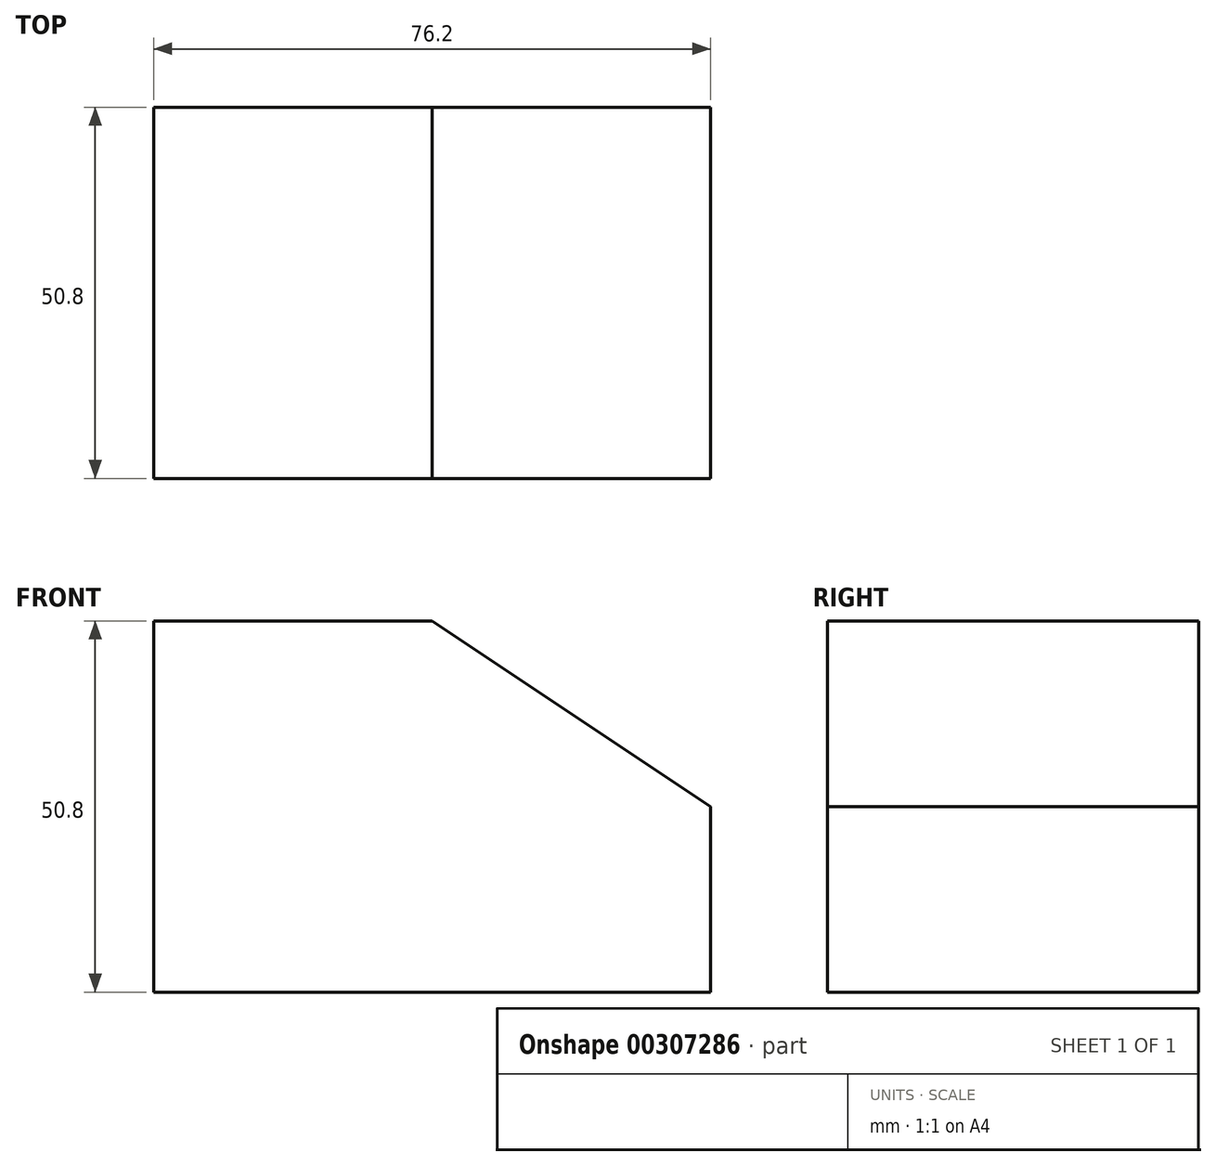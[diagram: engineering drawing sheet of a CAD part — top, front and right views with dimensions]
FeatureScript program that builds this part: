
annotation { "Feature Type Name" : "Feature", "Feature Type Description" : "" }
export const myFeature = defineFeature(function(context is Context, id is Id, definition is map)
    precondition{}
    {
        {
            var Q0;
            Q0=qCreatedBy(makeId("Front.planeOp"),FACE);
            var sketch = newSketch(context, id + "F0", { "sketchPlane" : qUnion([Q0])});
            skLineSegment(sketch, "E0", {"start": v(-40.75, -28.67) * mm, "end": v(-40.75, 22.13) * mm});
            skLineSegment(sketch, "E1", {"start": v(-40.75, 22.13) * mm, "end": v(-2.65, 22.13) * mm});
            skLineSegment(sketch, "E2", {"start": v(-2.65, 22.13) * mm, "end": v(35.45, -3.27) * mm});
            skLineSegment(sketch, "E3", {"start": v(35.45, -3.27) * mm, "end": v(35.45, -28.67) * mm});
            skLineSegment(sketch, "E4", {"start": v(35.45, -28.67) * mm, "end": v(-40.75, -28.67) * mm});
            skSolve(sketch);
        }
        {
            var Q0;
            Q0=makeQuery(id+"F0.imprint","IMPRINT",FACE,{"disambiguationData":[TD([[makeQuery(id+"F0.imprint","IMPRINT",EDGE,{"derivedFrom":sQuery(id+"F0.wireOp",EDGE,"E0")}),-1.0]])]});
            extrude(context, id + "F1", {"entities" : qUnion([Q0]), "depth" : 50.8 * mm});
        }
    });
